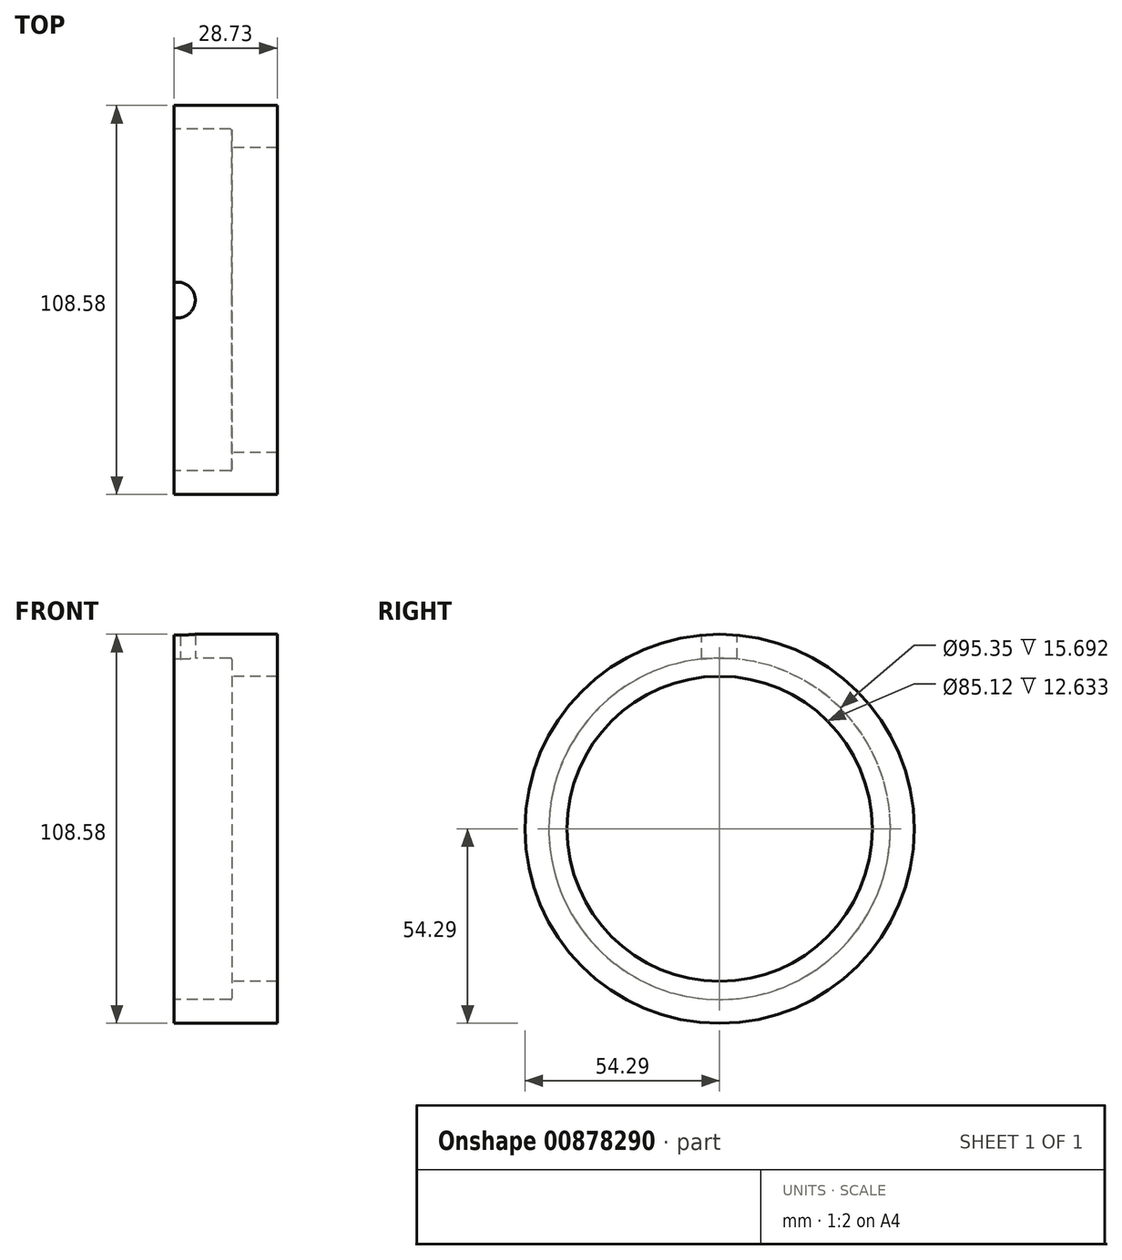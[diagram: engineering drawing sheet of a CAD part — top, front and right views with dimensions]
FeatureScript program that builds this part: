
annotation { "Feature Type Name" : "Feature", "Feature Type Description" : "" }
export const myFeature = defineFeature(function(context is Context, id is Id, definition is map)
    precondition{}
    {
        {
            var Q0;
            Q0=qCreatedBy(makeId("Front.planeOp"),FACE);
            var sketch = newSketch(context, id + "F0", { "sketchPlane" : qUnion([Q0])});
            skLineSegment(sketch, "E0", {"start": v(0, 54.3) * mm, "end": v(28.73, 54.3) * mm});
            skLineSegment(sketch, "E1", {"start": v(28.73, 54.3) * mm, "end": v(28.73, 42.56) * mm});
            skLineSegment(sketch, "E2", {"start": v(28.73, 42.56) * mm, "end": v(16.1, 42.56) * mm});
            skLineSegment(sketch, "E3", {"start": v(16.1, 42.56) * mm, "end": v(16.1, 47.68) * mm});
            skLineSegment(sketch, "E4", {"start": v(16.1, 47.68) * mm, "end": v(0, 47.68) * mm});
            skLineSegment(sketch, "E5", {"start": v(0, 47.68) * mm, "end": v(0, 54.3) * mm});
            skLineSegment(sketch, "E6", {"start": v(0, 0) * mm, "end": v(28.73, 0) * mm});
            skSolve(sketch);
        }
        {
            var Q0;
            Q0=makeQuery(id+"F0.imprint","IMPRINT",FACE,{"disambiguationData":[TD([[makeQuery(id+"F0.imprint","IMPRINT",EDGE,{"derivedFrom":sQuery(id+"F0.wireOp",EDGE,"E0")}),-1.0]])]});
            var Q1;
            Q1=sQuery(id+"F0.wireOp",EDGE,"E6");
            revolve(context, id + "F1", {"surfaceOperationType" : NewSurfaceOperationType.NEW, "entities" : qUnion([Q0]), "axis" : qUnion([Q1]), "revolveType" : RevolveType.FULL});
        }
        {
            var Q0;
            Q0=qCreatedBy(makeId("Top.planeOp"),FACE);
            var sketch = newSketch(context, id + "F2", { "sketchPlane" : qUnion([Q0])});
            skLineSegment(sketch, "E7.bottom", {"start": v(7.07, 4.96) * mm, "end": v(-7.07, 4.96) * mm});
            skLineSegment(sketch, "E7.top", {"start": v(7.07, -4.96) * mm, "end": v(-7.07, -4.96) * mm});
            skLineSegment(sketch, "E7.left", {"start": v(7.07, 4.96) * mm, "end": v(7.07, -4.96) * mm});
            skLineSegment(sketch, "E7.right", {"start": v(-7.07, 4.96) * mm, "end": v(-7.07, -4.96) * mm});
            skPoint(sketch, "E7.middle", {"position": v(0, 0) * mm});
            skArc(sketch, "E8", {"start": v(0, -4.96) * mm, "mid": v(5.87, 0) * mm, "end": v(0, 4.96) * mm});
            skSolve(sketch);
        }
        {
            var Q0;
            {var subQ0=sQuery(id+"F2.wireOp",EDGE,"E7.right");Q0=makeQuery(id+"F2.imprint","IMPRINT",FACE,{"disambiguationData":[TD([[makeQuery(id+"F2.imprint","IMPRINT",EDGE,{"derivedFrom":subQ0}),1.0]])]});}
            extrude(context, id + "F3", {"entities" : qUnion([Q0]), "operationType" : NewBodyOperationType.REMOVE, "depth" : 73.66 * mm, "offsetDistance" : 25.4 * mm});
        }
        {
            var Q0;
            Q0=makeQuery(id+"F1.opRevolve","SWEPT_EDGE",EDGE,{"disambiguationData":[OSD([sQuery(id+"F0.wireOp",EDGE,"E3"),sQuery(id+"F0.wireOp",EDGE,"E4")])]});
            fillet(context, id + "F4", {"entities" : qUnion([Q0]), "radius" : 0.4 * mm, "tangentPropagation" : true, "allowEdgeOverflow" : false});
        }
    });
